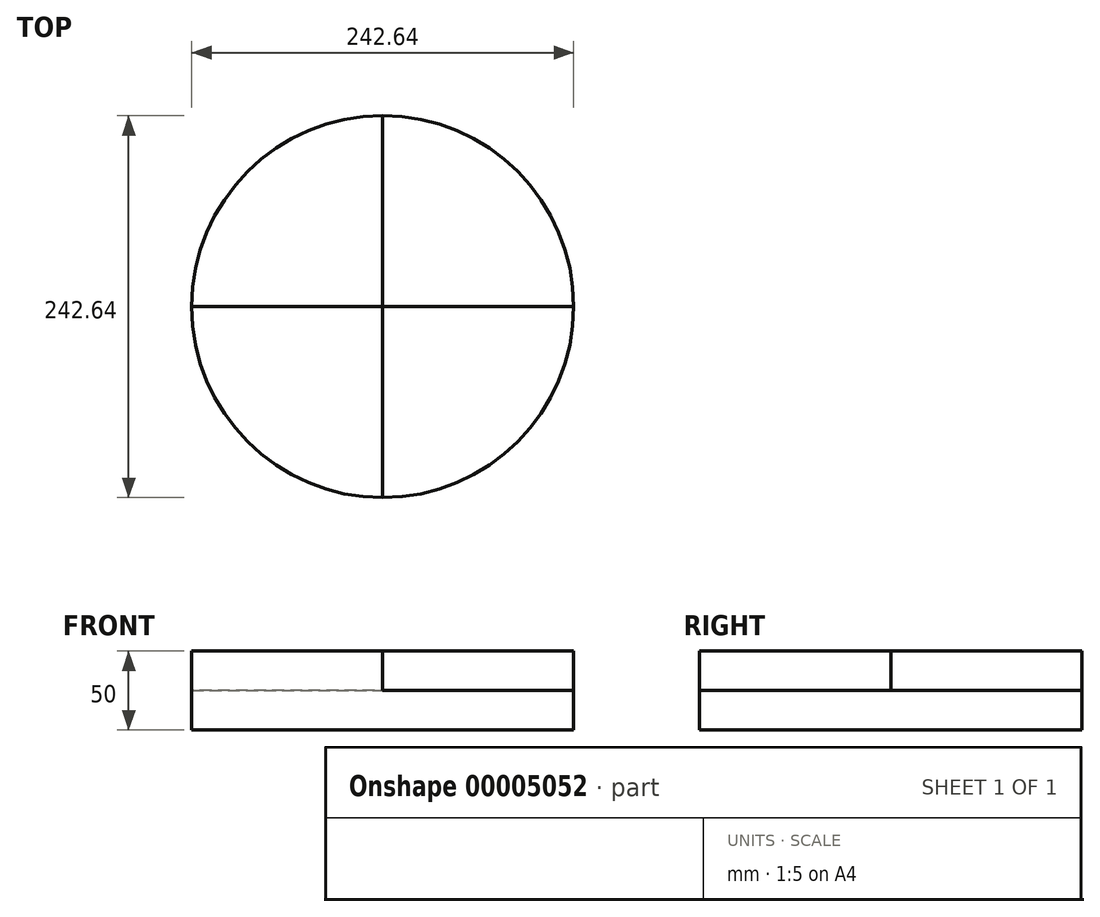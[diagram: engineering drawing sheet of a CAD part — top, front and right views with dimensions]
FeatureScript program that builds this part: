
annotation { "Feature Type Name" : "Feature", "Feature Type Description" : "" }
export const myFeature = defineFeature(function(context is Context, id is Id, definition is map)
    precondition{}
    {
        {
            var Q0;
            Q0=qCreatedBy(makeId("Top.planeOp"),FACE);
            var sketch = newSketch(context, id + "F0", { "sketchPlane" : qUnion([Q0])});
            skCircle(sketch, "E0", {"center": v(0, 0) * mm, "radius": 121.32 * mm});
            skLineSegment(sketch, "E1", {"start": v(0, 121.32) * mm, "end": v(0, -121.32) * mm});
            skLineSegment(sketch, "E2", {"start": v(-121.32, 0) * mm, "end": v(121.32, 0) * mm});
            skSolve(sketch);
        }
        {
            var Q0;
            Q0 = qSketchRegion(id + "F0", true);
            extrude(context, id + "F1", {"entities" : qUnion([Q0]), "oppositeDirection" : true, "depth" : 25 * mm});
        }
        {
            var Q0;
            {var subQ1=sQuery(id+"F0.wireOp",EDGE,"E1");var subQ3=sQuery(id+"F0.wireOp",EDGE,"E0");var subQ5=makeQuery(id+"F0.imprint","INTERSECT",VERTEX,{"disambiguationData":[OD(1.0)],"derivedFrom":[subQ3,subQ1]});Q0=makeQuery(id+"F0.imprint","IMPRINT",FACE,{"disambiguationData":[TD([[makeQuery(id+"F0.imprint","IMPRINT",EDGE,{"disambiguationData":[TD([[subQ5,1.0]])],"derivedFrom":subQ3}),1.0]])]});}
            extrude(context, id + "F2", {"entities" : qUnion([Q0]), "operationType" : NewBodyOperationType.ADD, "depth" : 25 * mm});
        }
        {
            var Q0;
            {var subQ1=sQuery(id+"F0.wireOp",EDGE,"E1");var subQ3=sQuery(id+"F0.wireOp",EDGE,"E0");var subQ5=makeQuery(id+"F0.imprint","INTERSECT",VERTEX,{"disambiguationData":[OD(0.0)],"derivedFrom":[subQ3,subQ1]});Q0=makeQuery(id+"F0.imprint","IMPRINT",FACE,{"disambiguationData":[TD([[makeQuery(id+"F0.imprint","IMPRINT",EDGE,{"disambiguationData":[TD([[subQ5,1.0]])],"derivedFrom":subQ3}),1.0]])]});}
            extrude(context, id + "F3", {"entities" : qUnion([Q0]), "depth" : 25 * mm});
        }
    });
